# Revit family: Gira_014001
name_source: partatom
category: Electrical Fixtures
revit_build: Autodesk Revit 2017 (Build: 20160225_1515(x64)
units: mm (PartAtom-declared; Revit-internal decimal feet)

## family parameters
Cut with Voids When Loaded = No
Host = Face
Maintain Annotation Orientation = Yes
Part Type = Normal
Room Calculation Point = No
Round Connector Dimension = Use Diameter
Shared = No

## types (1)
- Hotel-Card-Taster Wechsler (bel.) BSF System 55 Cremeweiß
    Anzahl der Betätigungswippen = 1
    Aufdruck = ohne
    Ausführung = Einzeltaster
    Ausführung der Oberfläche = glänzend
    Available = Yes
    Bedienungsart = Hotelcard
    Befestigungsart = Krallen-/Schraubbefestigung
    Bemessungsstrom = 10 Ampere
    Category = Taster
    Data sheet (1) = https://katalog.gira.de
    Default Elevation = 1219 mm
    Farbe = cremeweiß (elektroweiß)
    GTIN = 4010337140016
    Geeignet für Schutzart (IP) = IP20
    HAN = 014001
    Halogenfrei = Yes
    HeinzeBIM = https://bimportal.heinze.de
    Kontakte = 1 Wechsler
    Manufacturer URL = https://www.gira.de
    Mit Beleuchtung = No
    Model = Sys55_Komplettgerät_Schalten und Tasten
    Montageart = unter Putz
    Name = Hotel-Card-Taster Wechsler (bel.) BSF System 55 Cremeweiß
    Nennspannung = 250 Volt
    Oberfläche = sonstige
    RAL-Nummer (ähnlich) = 1013
    Region = DE
    Rückmeldekontakt = No
    Textfeld/Beschriftungsfläche = Yes
    Transparent = No
    URL = http://katalog.gira.de
    Werkstoff = sonstige
    Werkstoffgüte = sonstige
    Zusammenstellung = Basiselement mit zentraler Abdeckplatte

## geometry (parser evidence)
native form markers: Blend x2, Sweep x12
no freeform markers — native parametric forms only
